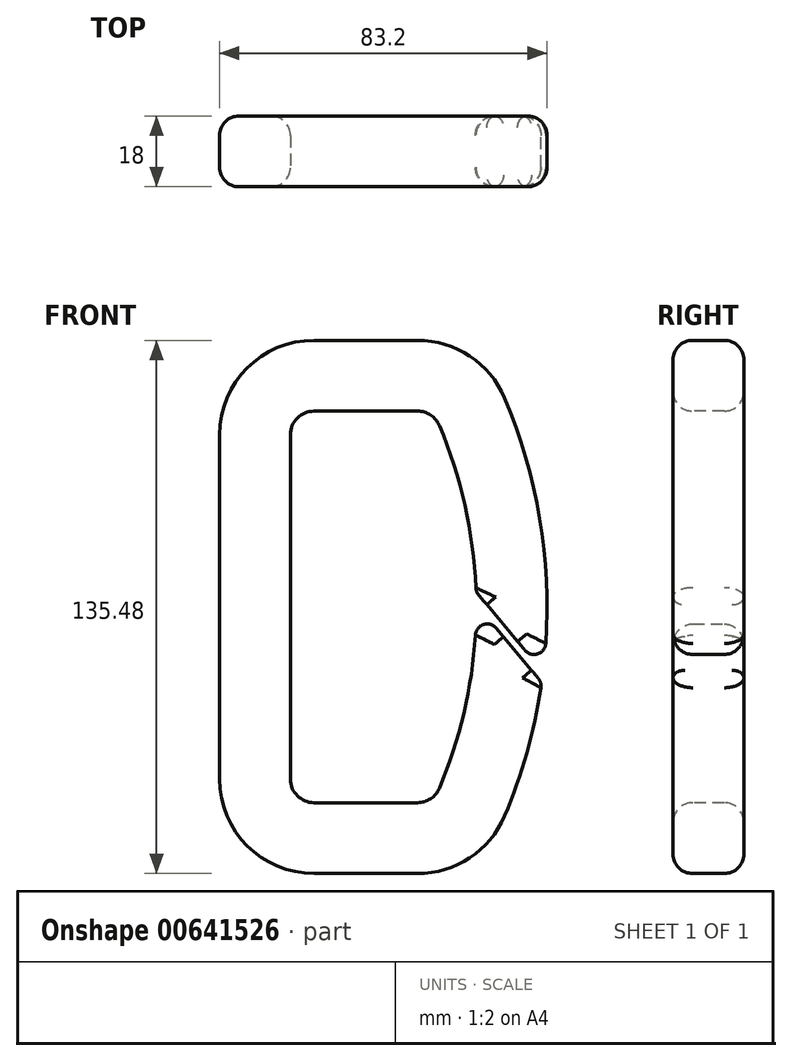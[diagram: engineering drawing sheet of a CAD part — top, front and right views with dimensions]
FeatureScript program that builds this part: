
annotation { "Feature Type Name" : "Feature", "Feature Type Description" : "" }
export const myFeature = defineFeature(function(context is Context, id is Id, definition is map)
    precondition{}
    {
        {
            var Q0;
            Q0=qCreatedBy(makeId("Front.planeOp"),FACE);
            var sketch = newSketch(context, id + "F0", { "sketchPlane" : qUnion([Q0])});
            skLineSegment(sketch, "E0", {"start": v(15.9, 58.74) * mm, "end": v(-10.4, 58.74) * mm});
            skLineSegment(sketch, "E1", {"start": v(-25.4, 43.74) * mm, "end": v(-25.4, -43.74) * mm});
            skLineSegment(sketch, "E2", {"start": v(-10.4, -58.74) * mm, "end": v(15.9, -58.74) * mm});
            skArc(sketch, "E3", {"start": v(29.72, -49.6) * mm, "mid": v(39.8, 0) * mm, "end": v(29.72, 49.6) * mm});
            skLineSegment(sketch, "E4", {"start": v(0, 0) * mm, "end": v(-25.4, 0) * mm, "construction": true});
            skPoint(sketch, "E5.visualSharp", {"position": v(-25.4, 58.74) * mm});
            skArc(sketch, "E5.filletArc", {"start": v(-10.4, 58.74) * mm, "mid": v(-21, 54.34) * mm, "end": v(-25.4, 43.74) * mm});
            skPoint(sketch, "E6.visualSharp", {"position": v(-25.4, -58.74) * mm});
            skArc(sketch, "E6.filletArc", {"start": v(-25.4, -43.74) * mm, "mid": v(-21, -54.34) * mm, "end": v(-10.4, -58.74) * mm});
            skPoint(sketch, "E7.visualSharp", {"position": v(25.4, 58.74) * mm});
            skArc(sketch, "E7.filletArc", {"start": v(29.72, 49.6) * mm, "mid": v(24.19, 56.24) * mm, "end": v(15.9, 58.74) * mm});
            skPoint(sketch, "E8.visualSharp", {"position": v(25.4, -58.74) * mm});
            skArc(sketch, "E8.filletArc", {"start": v(15.9, -58.74) * mm, "mid": v(24.19, -56.24) * mm, "end": v(29.72, -49.6) * mm});
            skSolve(sketch);
        }
        {
            var Q0;
            Q0=qCreatedBy(makeId("Top.planeOp"),FACE);
            var sketch = newSketch(context, id + "F1", { "sketchPlane" : qUnion([Q0])});
            skPoint(sketch, "E9.0", {"position": v(-25.4, 0) * mm});
            skLineSegment(sketch, "E10.bottom", {"start": v(-29.4, 9) * mm, "end": v(-21.4, 9) * mm});
            skLineSegment(sketch, "E10.top", {"start": v(-29.4, -9) * mm, "end": v(-21.4, -9) * mm});
            skLineSegment(sketch, "E10.left", {"start": v(-34.4, 4) * mm, "end": v(-34.4, -4) * mm});
            skLineSegment(sketch, "E10.right", {"start": v(-16.4, 4) * mm, "end": v(-16.4, -4) * mm});
            skPoint(sketch, "E11.visualSharp", {"position": v(-34.4, 9) * mm});
            skArc(sketch, "E11.filletArc", {"start": v(-29.4, 9) * mm, "mid": v(-32.94, 7.54) * mm, "end": v(-34.4, 4) * mm});
            skPoint(sketch, "E12.visualSharp", {"position": v(-34.4, -9) * mm});
            skArc(sketch, "E12.filletArc", {"start": v(-34.4, -4) * mm, "mid": v(-32.94, -7.54) * mm, "end": v(-29.4, -9) * mm});
            skPoint(sketch, "E13.visualSharp", {"position": v(-16.4, -9) * mm});
            skArc(sketch, "E13.filletArc", {"start": v(-21.4, -9) * mm, "mid": v(-17.86, -7.54) * mm, "end": v(-16.4, -4) * mm});
            skPoint(sketch, "E14.visualSharp", {"position": v(-16.4, 9) * mm});
            skArc(sketch, "E14.filletArc", {"start": v(-16.4, 4) * mm, "mid": v(-17.86, 7.54) * mm, "end": v(-21.4, 9) * mm});
            skSolve(sketch);
        }
        {
            var Q0;
            Q0=makeQuery(id+"F1.imprint","IMPRINT",FACE,{"disambiguationData":[TD([[makeQuery(id+"F1.imprint","IMPRINT",EDGE,{"derivedFrom":sQuery(id+"F1.wireOp",EDGE,"b33b04e6-907e-499e-afa9-051d44160396")}),1.0]])]});
            var Q1;
            Q1=makeQuery(id+"F1.imprint","IMPRINT",FACE,{"disambiguationData":[TD([[makeQuery(id+"F1.imprint","IMPRINT",EDGE,{"derivedFrom":sQuery(id+"F1.wireOp",EDGE,"E10.bottom")}),-1.0]])]});
            var Q2;
            Q2=sQuery(id+"F0.wireOp",EDGE,"E1");
            var Q3;
            Q3=sQuery(id+"F0.wireOp",EDGE,"E6.filletArc");
            var Q4;
            Q4=sQuery(id+"F0.wireOp",EDGE,"E2");
            var Q5;
            Q5=sQuery(id+"F0.wireOp",EDGE,"E8.filletArc");
            var Q6;
            Q6=sQuery(id+"F0.wireOp",EDGE,"E3");
            var Q7;
            Q7=sQuery(id+"F0.wireOp",EDGE,"E5.filletArc");
            var Q8;
            Q8=sQuery(id+"F0.wireOp",EDGE,"E0");
            var Q9;
            Q9=sQuery(id+"F0.wireOp",EDGE,"E7.filletArc");
            sweep(context, id + "F2", {"profiles" : qUnion([Q0, Q1]), "path" : qUnion([Q2, Q3, Q4, Q5, Q6, Q7, Q8, Q9])});
        }
        {
            var Q0;
            Q0=qCreatedBy(makeId("Front.planeOp"),FACE);
            var sketch = newSketch(context, id + "F3", { "sketchPlane" : qUnion([Q0])});
            skLineSegment(sketch, "E15", {"start": v(83.23, -61.83) * mm, "end": v(0, 37.36) * mm});
            skLineSegment(sketch, "E16", {"start": v(83.23, -61.83) * mm, "end": v(84.76, -60.55) * mm});
            skLineSegment(sketch, "E17", {"start": v(1.53, 38.64) * mm, "end": v(84.76, -60.55) * mm});
            skLineSegment(sketch, "E18", {"start": v(1.53, 38.64) * mm, "end": v(0, 37.36) * mm});
            skLineSegment(sketch, "E19", {"start": v(15.9, 49.74) * mm, "end": v(-12.84, 49.74) * mm});
            skLineSegment(sketch, "E20", {"start": v(-10.4, 67.74) * mm, "end": v(15.9, 67.74) * mm});
            skLineSegment(sketch, "E21", {"start": v(1.53, 49.74) * mm, "end": v(1.53, 38.64) * mm});
            skSolve(sketch);
        }
        {
            var Q0;
            Q0 = qSketchRegion(id + "F3", true);
            extrude(context, id + "F4", {"entities" : qUnion([Q0]), "operationType" : NewBodyOperationType.REMOVE, "endBound" : BoundingType.SYMMETRIC, "oppositeDirection" : true, "depth" : 50 * mm, "offsetDistance" : 25 * mm});
        }
        {
            var Q0;
            Q0=makeQuery(id+"F4.boolean.opBoolean","INTERSECT",EDGE,{"derivedFrom":[makeQuery(id+"F2.opSweep","SWEPT_FACE",FACE,{"disambiguationData":[OSD([sQuery(id+"F0.wireOp",EDGE,"E3"),sQuery(id+"F1.wireOp",EDGE,"b33b04e6-907e-499e-afa9-051d44160396")])]}),makeQuery(id+"F4.opExtrude","SWEPT_FACE",FACE,{"disambiguationData":[OSD([sQuery(id+"F3.wireOp",EDGE,"E17")])]})]});
            var Q1;
            Q1=makeQuery(id+"F4.boolean.opBoolean","INTERSECT",EDGE,{"derivedFrom":[makeQuery(id+"F2.opSweep","SWEPT_FACE",FACE,{"disambiguationData":[OSD([sQuery(id+"F0.wireOp",EDGE,"E3"),sQuery(id+"F1.wireOp",EDGE,"b33b04e6-907e-499e-afa9-051d44160396")])]}),makeQuery(id+"F4.opExtrude","SWEPT_FACE",FACE,{"disambiguationData":[OSD([sQuery(id+"F3.wireOp",EDGE,"E15")])]})]});
            fillet(context, id + "F5", {"entities" : qUnion([Q0, Q1]), "radius" : 3 * mm, "tangentPropagation" : true, "allowEdgeOverflow" : false});
        }
    });
